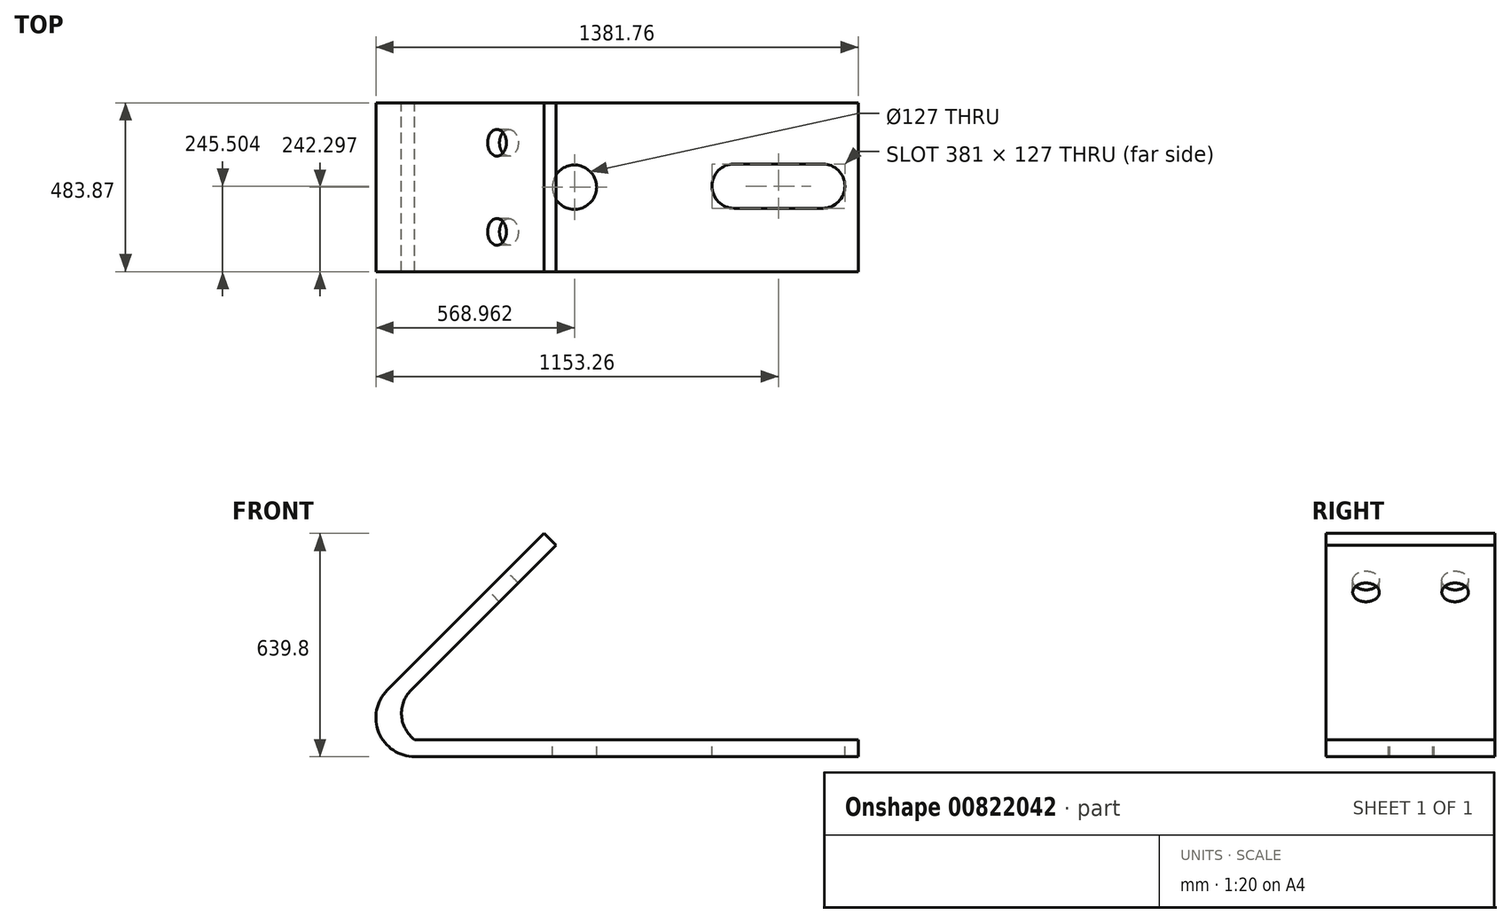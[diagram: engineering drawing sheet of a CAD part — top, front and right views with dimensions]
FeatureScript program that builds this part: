
annotation { "Feature Type Name" : "Feature", "Feature Type Description" : "" }
export const myFeature = defineFeature(function(context is Context, id is Id, definition is map)
    precondition{}
    {
        {
            var Q0;
            Q0=qCreatedBy(makeId("Front.planeOp"),FACE);
            var sketch = newSketch(context, id + "F0", { "sketchPlane" : qUnion([Q0])});
            skLineSegment(sketch, "E0", {"start": v(-39.9, 284.33) * mm, "end": v(-488.91, -164.68) * mm});
            skLineSegment(sketch, "E1", {"start": v(-409.89, -355.47) * mm, "end": v(860.11, -355.47) * mm});
            skArc(sketch, "E2", {"start": v(-488.91, -164.68) * mm, "mid": v(-513.14, -286.48) * mm, "end": v(-409.89, -355.47) * mm});
            skLineSegment(sketch, "E3", {"start": v(860.11, -355.47) * mm, "end": v(860.11, -307.2) * mm});
            skLineSegment(sketch, "E4", {"start": v(-39.9, 284.33) * mm, "end": v(-5.78, 250.2) * mm});
            skLineSegment(sketch, "E5", {"start": v(-5.78, 250.2) * mm, "end": v(-420.66, -164.68) * mm});
            skLineSegment(sketch, "E6", {"start": v(860.11, -307.2) * mm, "end": v(-409.89, -307.2) * mm});
            skArc(sketch, "E7", {"start": v(-420.66, -164.68) * mm, "mid": v(-448, -238.42) * mm, "end": v(-409.89, -307.2) * mm});
            skSolve(sketch);
        }
        {
            var Q0;
            Q0=makeQuery(id+"F0.imprint","IMPRINT",FACE,{"disambiguationData":[TD([[makeQuery(id+"F0.imprint","IMPRINT",EDGE,{"derivedFrom":sQuery(id+"F0.wireOp",EDGE,"E0")}),1.0]])]});
            extrude(context, id + "F1", {"entities" : qUnion([Q0]), "depth" : 483.87 * mm, "offsetDistance" : 25.4 * mm});
        }
        {
            var Q0;
            Q0=makeQuery(id+"F1.opExtrude","SWEPT_FACE",FACE,{"disambiguationData":[OSD([sQuery(id+"F0.wireOp",EDGE,"E6")])]});
            var sketch = newSketch(context, id + "F2", { "sketchPlane" : qUnion([Q0])});
            skCircle(sketch, "E8", {"center": v(47.31, -241.57) * mm, "radius": 63.5 * mm});
            skLineSegment(sketch, "E9", {"start": v(504.61, -174.87) * mm, "end": v(758.61, -174.87) * mm});
            skLineSegment(sketch, "E10", {"start": v(504.61, -301.87) * mm, "end": v(758.61, -301.87) * mm});
            skArc(sketch, "E11", {"start": v(504.61, -174.87) * mm, "mid": v(441.11, -238.37) * mm, "end": v(504.61, -301.87) * mm});
            skArc(sketch, "E12", {"start": v(758.61, -301.87) * mm, "mid": v(822.11, -238.37) * mm, "end": v(758.61, -174.87) * mm});
            skSolve(sketch);
        }
        {
            var Q0;
            Q0=makeQuery(id+"F2.imprint","IMPRINT",FACE,{"disambiguationData":[TD([[makeQuery(id+"F2.imprint","IMPRINT",EDGE,{"derivedFrom":sQuery(id+"F2.wireOp",EDGE,"E8")}),1.0]])]});
            var Q1;
            Q1=makeQuery(id+"F2.imprint","IMPRINT",FACE,{"disambiguationData":[TD([[makeQuery(id+"F2.imprint","IMPRINT",EDGE,{"derivedFrom":sQuery(id+"F2.wireOp",EDGE,"E9")}),-1.0]])]});
            extrude(context, id + "F3", {"entities" : qUnion([Q0, Q1]), "operationType" : NewBodyOperationType.REMOVE, "oppositeDirection" : true, "depth" : 307.34 * mm, "offsetDistance" : 25.4 * mm});
        }
        {
            var Q0;
            Q0=makeQuery(id+"F1.opExtrude","SWEPT_FACE",FACE,{"disambiguationData":[OSD([sQuery(id+"F0.wireOp",EDGE,"E0")])]});
            var sketch = newSketch(context, id + "F4", { "sketchPlane" : qUnion([Q0])});
            skCircle(sketch, "E13", {"center": v(114.3, -17.66) * mm, "radius": 38.1 * mm});
            skCircle(sketch, "E14", {"center": v(369.57, -17.66) * mm, "radius": 38.1 * mm});
            skSolve(sketch);
        }
        {
            var Q0;
            Q0=makeQuery(id+"F4.imprint","IMPRINT",FACE,{"disambiguationData":[TD([[makeQuery(id+"F4.imprint","IMPRINT",EDGE,{"derivedFrom":sQuery(id+"F4.wireOp",EDGE,"E13")}),1.0]])]});
            var Q1;
            Q1=makeQuery(id+"F4.imprint","IMPRINT",FACE,{"disambiguationData":[TD([[makeQuery(id+"F4.imprint","IMPRINT",EDGE,{"derivedFrom":sQuery(id+"F4.wireOp",EDGE,"E14")}),1.0]])]});
            extrude(context, id + "F5", {"entities" : qUnion([Q0, Q1]), "operationType" : NewBodyOperationType.REMOVE, "oppositeDirection" : true, "depth" : 170.18 * mm, "offsetDistance" : 25.4 * mm});
        }
    });
